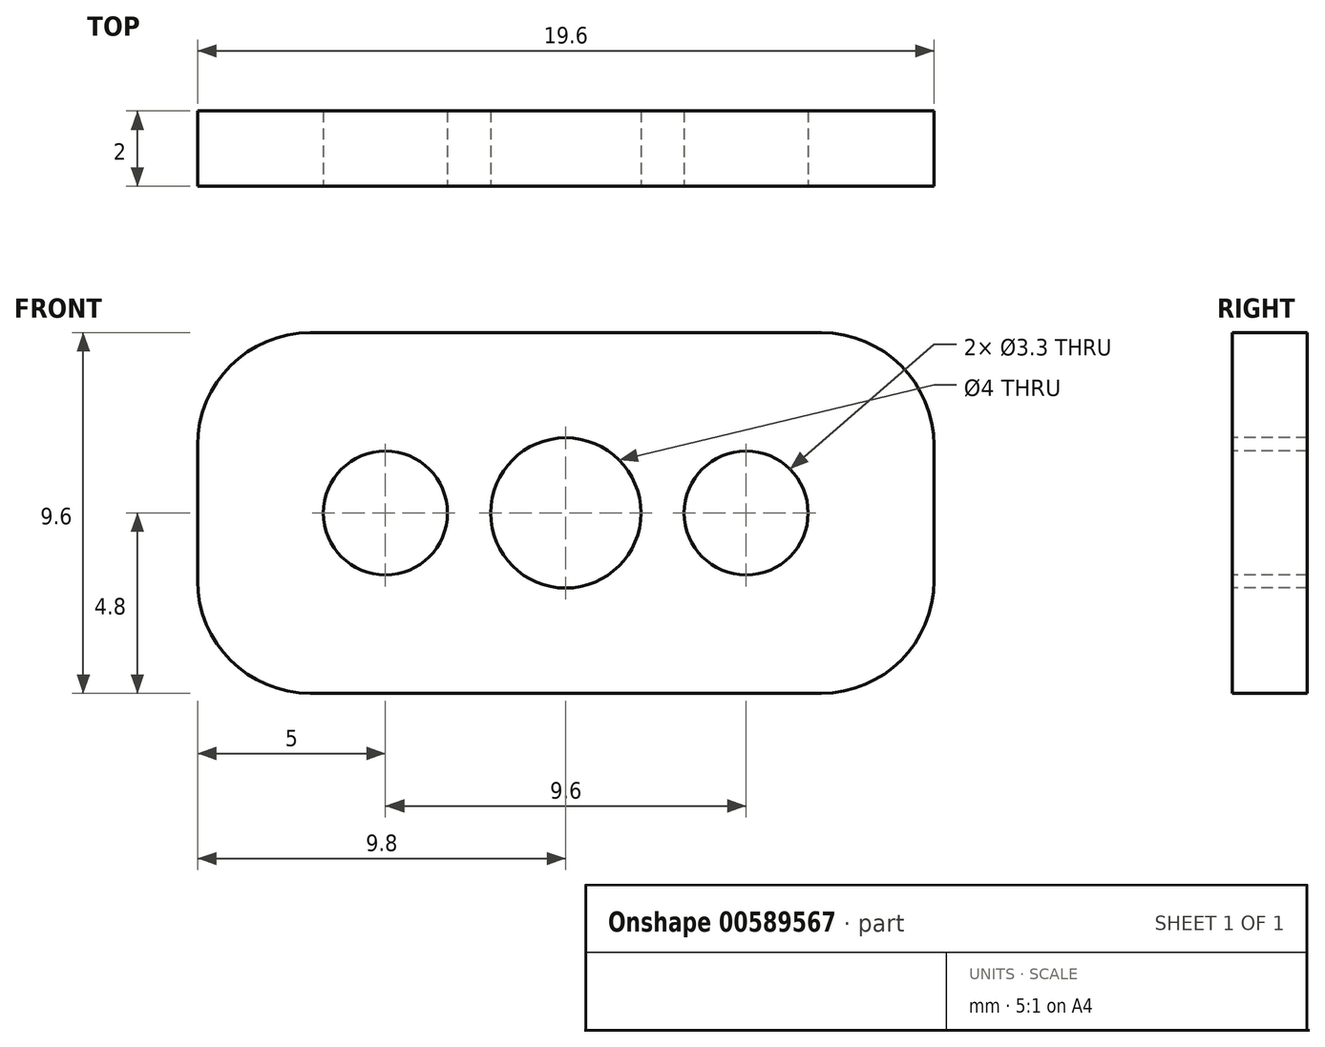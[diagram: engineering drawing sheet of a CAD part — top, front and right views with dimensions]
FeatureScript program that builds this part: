
annotation { "Feature Type Name" : "Feature", "Feature Type Description" : "" }
export const myFeature = defineFeature(function(context is Context, id is Id, definition is map)
    precondition{}
    {
        {
            var Q0;
            Q0=qCreatedBy(makeId("Front.planeOp"),FACE);
            var sketch = newSketch(context, id + "F0", { "sketchPlane" : qUnion([Q0])});
            skLineSegment(sketch, "E0.bottom", {"start": v(0, 0) * mm, "end": v(19.6, 0) * mm});
            skLineSegment(sketch, "E0.top", {"start": v(0, 9.6) * mm, "end": v(19.6, 9.6) * mm});
            skLineSegment(sketch, "E0.left", {"start": v(0, 0) * mm, "end": v(0, 9.6) * mm});
            skLineSegment(sketch, "E0.right", {"start": v(19.6, 0) * mm, "end": v(19.6, 9.6) * mm});
            skSolve(sketch);
        }
        {
            var Q0;
            Q0=makeQuery(id+"F0.imprint","IMPRINT",FACE,{"disambiguationData":[TD([[makeQuery(id+"F0.imprint","IMPRINT",EDGE,{"derivedFrom":sQuery(id+"F0.wireOp",EDGE,"E0.bottom")}),1.0]])]});
            extrude(context, id + "F1", {"entities" : qUnion([Q0]), "depth" : 2 * mm, "offsetDistance" : 25 * mm});
        }
        {
            var Q0;
            Q0=makeQuery(id+"F1.opExtrude","CAP_FACE",FACE,{"disambiguationData":[OSD([sQuery(id+"F0.wireOp",EDGE,"E0.bottom"),sQuery(id+"F0.wireOp",EDGE,"E0.top"),sQuery(id+"F0.wireOp",EDGE,"E0.left"),sQuery(id+"F0.wireOp",EDGE,"E0.right")])],"isStart":false});
            var sketch = newSketch(context, id + "F2", { "sketchPlane" : qUnion([Q0])});
            skCircle(sketch, "E1", {"center": v(9.8, 4.8) * mm, "radius": 2 * mm});
            skSolve(sketch);
        }
        {
            var Q0;
            Q0=makeQuery(id+"F2.imprint","IMPRINT",FACE,{"disambiguationData":[TD([[makeQuery(id+"F2.imprint","IMPRINT",EDGE,{"derivedFrom":sQuery(id+"F2.wireOp",EDGE,"E1")}),1.0]])]});
            extrude(context, id + "F3", {"entities" : qUnion([Q0]), "operationType" : NewBodyOperationType.REMOVE, "oppositeDirection" : true, "depth" : 3 * mm, "offsetDistance" : 25 * mm});
        }
        {
            var Q0;
            Q0=makeQuery(id+"F1.opExtrude","CAP_FACE",FACE,{"disambiguationData":[OSD([sQuery(id+"F0.wireOp",EDGE,"E0.bottom"),sQuery(id+"F0.wireOp",EDGE,"E0.top"),sQuery(id+"F0.wireOp",EDGE,"E0.left"),sQuery(id+"F0.wireOp",EDGE,"E0.right")])],"isStart":false});
            var sketch = newSketch(context, id + "F4", { "sketchPlane" : qUnion([Q0])});
            skCircle(sketch, "E2", {"center": v(5, 4.8) * mm, "radius": 1.65 * mm});
            skSolve(sketch);
        }
        {
            var Q0;
            Q0=makeQuery(id+"F4.imprint","IMPRINT",FACE,{"disambiguationData":[TD([[makeQuery(id+"F4.imprint","IMPRINT",EDGE,{"derivedFrom":sQuery(id+"F4.wireOp",EDGE,"E2")}),-1.0]])]});
            var sketch = newSketch(context, id + "F5", { "sketchPlane" : qUnion([Q0])});
            skCircle(sketch, "E3", {"center": v(14.6, 4.8) * mm, "radius": 1.65 * mm});
            skSolve(sketch);
        }
        {
            var Q0;
            Q0=makeQuery(id+"F4.imprint","IMPRINT",FACE,{"disambiguationData":[TD([[makeQuery(id+"F4.imprint","IMPRINT",EDGE,{"derivedFrom":sQuery(id+"F4.wireOp",EDGE,"E2")}),1.0]])]});
            extrude(context, id + "F6", {"entities" : qUnion([Q0]), "operationType" : NewBodyOperationType.REMOVE, "oppositeDirection" : true, "depth" : 3 * mm, "offsetDistance" : 25 * mm});
        }
        {
            var Q0;
            Q0=makeQuery(id+"F5.imprint","IMPRINT",FACE,{"disambiguationData":[TD([[makeQuery(id+"F5.imprint","IMPRINT",EDGE,{"derivedFrom":sQuery(id+"F5.wireOp",EDGE,"E3")}),1.0]])]});
            extrude(context, id + "F7", {"entities" : qUnion([Q0]), "operationType" : NewBodyOperationType.REMOVE, "oppositeDirection" : true, "depth" : 3 * mm, "offsetDistance" : 25 * mm});
        }
        {
            var Q0;
            Q0=makeQuery(id+"F1.opExtrude","SWEPT_EDGE",EDGE,{"disambiguationData":[OSD([sQuery(id+"F0.wireOp",EDGE,"E0.top"),sQuery(id+"F0.wireOp",EDGE,"E0.right")])]});
            var Q1;
            Q1=makeQuery(id+"F1.opExtrude","SWEPT_EDGE",EDGE,{"disambiguationData":[OSD([sQuery(id+"F0.wireOp",EDGE,"E0.top"),sQuery(id+"F0.wireOp",EDGE,"E0.left")])]});
            var Q2;
            Q2=makeQuery(id+"F1.opExtrude","SWEPT_EDGE",EDGE,{"disambiguationData":[OSD([sQuery(id+"F0.wireOp",EDGE,"E0.bottom"),sQuery(id+"F0.wireOp",EDGE,"E0.left")])]});
            var Q3;
            Q3=makeQuery(id+"F1.opExtrude","SWEPT_EDGE",EDGE,{"disambiguationData":[OSD([sQuery(id+"F0.wireOp",EDGE,"E0.bottom"),sQuery(id+"F0.wireOp",EDGE,"E0.right")])]});
            fillet(context, id + "F8", {"entities" : qUnion([Q0, Q1, Q2, Q3]), "radius" : 3 * mm, "tangentPropagation" : true, "allowEdgeOverflow" : false});
        }
    });
